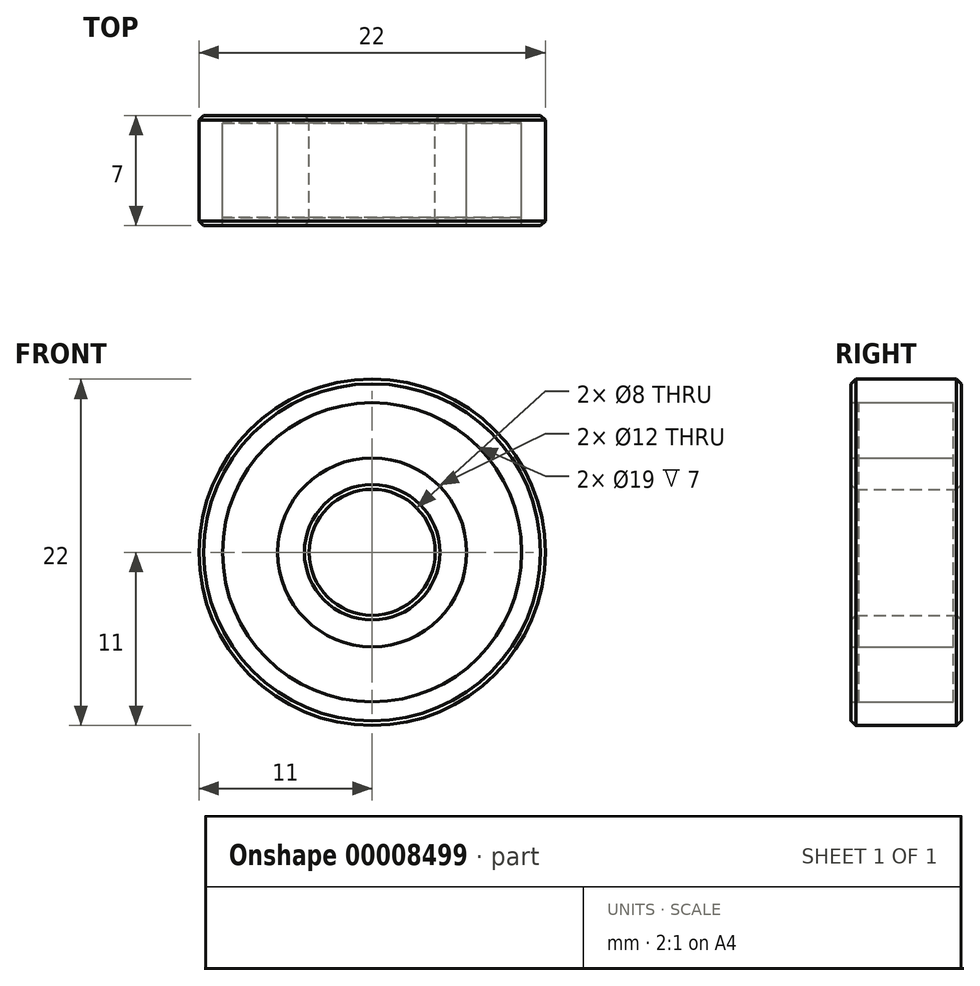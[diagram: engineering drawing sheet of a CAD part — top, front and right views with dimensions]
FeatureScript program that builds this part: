
annotation { "Feature Type Name" : "Feature", "Feature Type Description" : "" }
export const myFeature = defineFeature(function(context is Context, id is Id, definition is map)
    precondition{}
    {
        {
            var Q0;
            Q0=qCreatedBy(makeId("Front.planeOp"),FACE);
            var sketch = newSketch(context, id + "F0", { "sketchPlane" : qUnion([Q0])});
            skCircle(sketch, "E0", {"center": v(0, 0) * mm, "radius": 6 * mm});
            skCircle(sketch, "E1", {"center": v(0, 0) * mm, "radius": 4 * mm});
            skCircle(sketch, "E2", {"center": v(0, 0) * mm, "radius": 11 * mm});
            skCircle(sketch, "E3", {"center": v(0, 0) * mm, "radius": 9.5 * mm});
            skSolve(sketch);
        }
        {
            var Q0;
            Q0=makeQuery(id+"F0.imprint","IMPRINT",FACE,{"disambiguationData":[TD([[makeQuery(id+"F0.imprint","IMPRINT",EDGE,{"derivedFrom":sQuery(id+"F0.wireOp",EDGE,"E0")}),1.0]])]});
            var Q1;
            Q1=makeQuery(id+"F0.imprint","IMPRINT",FACE,{"disambiguationData":[TD([[makeQuery(id+"F0.imprint","IMPRINT",EDGE,{"derivedFrom":sQuery(id+"F0.wireOp",EDGE,"E2")}),1.0]])]});
            extrude(context, id + "F1", {"entities" : qUnion([Q0, Q1]), "endBound" : BoundingType.SYMMETRIC, "depth" : 7 * mm});
        }
        {
            var Q0;
            Q0=makeQuery(id+"F0.imprint","IMPRINT",FACE,{"disambiguationData":[TD([[makeQuery(id+"F0.imprint","IMPRINT",EDGE,{"derivedFrom":sQuery(id+"F0.wireOp",EDGE,"E0")}),-1.0]])]});
            extrude(context, id + "F2", {"entities" : qUnion([Q0]), "endBound" : BoundingType.SYMMETRIC, "depth" : 6 * mm});
        }
        {
            var Q0;
            Q0=makeQuery(id+"F1.opExtrude","SWEPT_FACE",FACE,{"disambiguationData":[OSD([sQuery(id+"F0.wireOp",EDGE,"E1")])]});
            var Q1;
            Q1=makeQuery(id+"F1.opExtrude","SWEPT_FACE",FACE,{"disambiguationData":[OSD([sQuery(id+"F0.wireOp",EDGE,"E2")])]});
            chamfer(context, id + "F3", {"entities" : qUnion([Q0, Q1]), "width" : 0.3 * mm, "tangentPropagation" : true});
        }
    });
